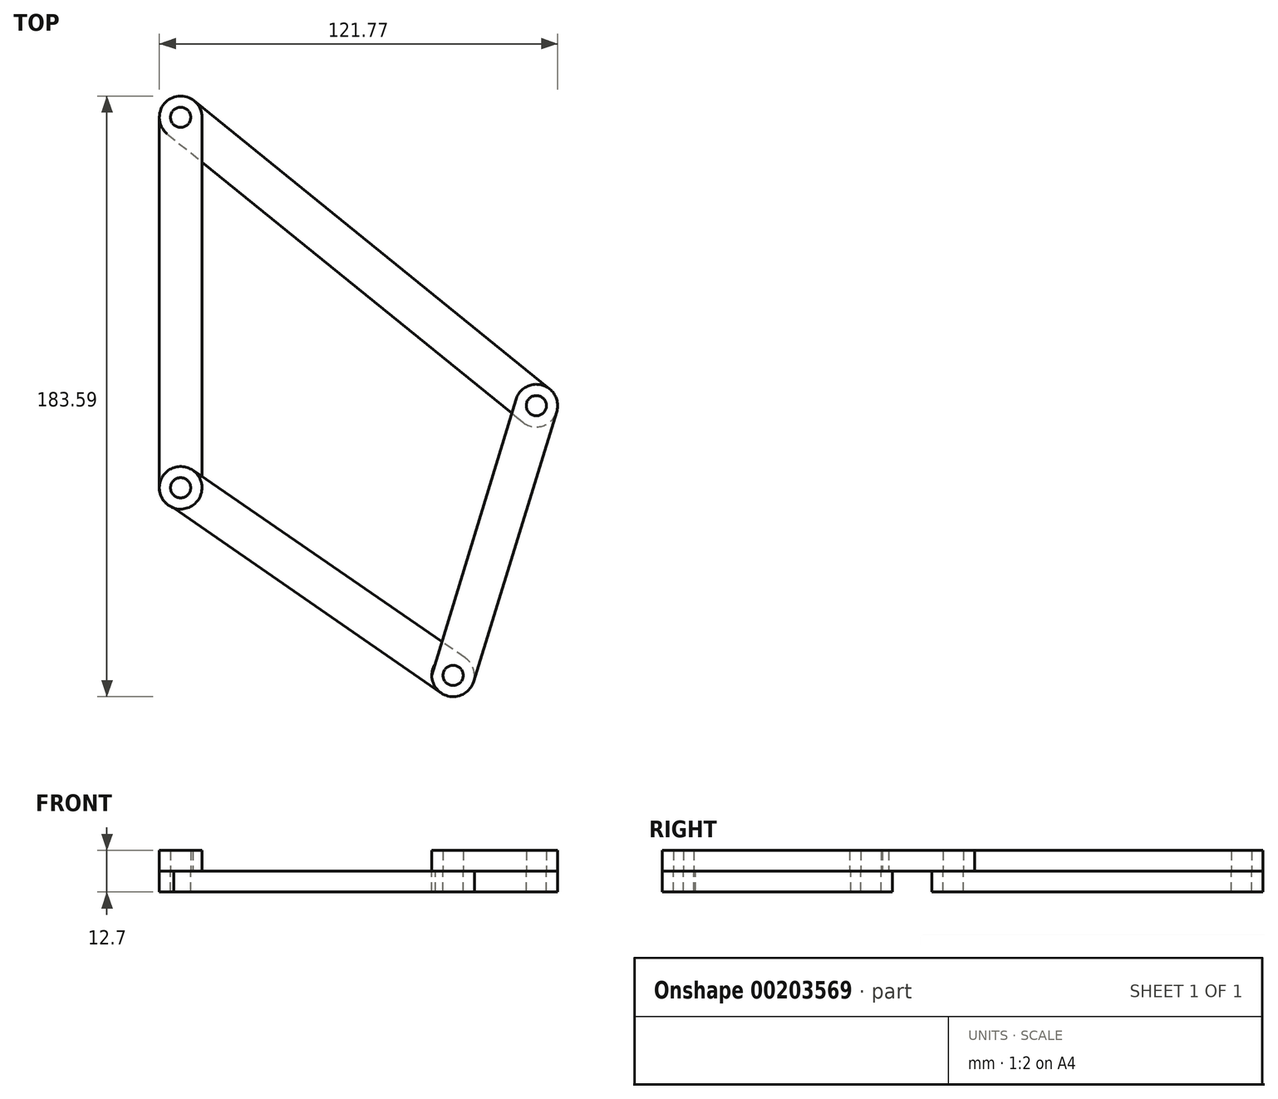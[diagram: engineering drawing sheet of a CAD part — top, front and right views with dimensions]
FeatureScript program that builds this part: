
annotation { "Feature Type Name" : "Feature", "Feature Type Description" : "" }
export const myFeature = defineFeature(function(context is Context, id is Id, definition is map)
    precondition{}
    {
        {
            var Q0;
            Q0=qCreatedBy(makeId("Top.planeOp"),FACE);
            var sketch = newSketch(context, id + "F0", { "sketchPlane" : qUnion([Q0])});
            skCircle(sketch, "E0", {"center": v(12.83, -29.92) * mm, "radius": 6.51 * mm});
            skCircle(sketch, "E1", {"center": v(-12.61, -112.37) * mm, "radius": 6.51 * mm});
            skCircle(sketch, "E2", {"center": v(-95.91, -55.04) * mm, "radius": 6.51 * mm});
            skCircle(sketch, "E3", {"center": v(-95.91, 58.2) * mm, "radius": 6.51 * mm});
            skLineSegment(sketch, "E4", {"start": v(-98.05, -61.2) * mm, "end": v(-16.32, -117.72) * mm});
            skLineSegment(sketch, "E5", {"start": v(-8.92, -107) * mm, "end": v(-92.22, -49.67) * mm});
            skLineSegment(sketch, "E6", {"start": v(-6.39, -114.29) * mm, "end": v(19.05, -31.84) * mm});
            skLineSegment(sketch, "E7", {"start": v(-19.12, -112.37) * mm, "end": v(6.6, -28.02) * mm});
            skLineSegment(sketch, "E8", {"start": v(16.93, -24.86) * mm, "end": v(-91.81, 63.26) * mm});
            skLineSegment(sketch, "E9", {"start": v(-100.01, 53.14) * mm, "end": v(8.72, -34.98) * mm});
            skLineSegment(sketch, "E10", {"start": v(-102.43, 58.2) * mm, "end": v(-102.43, -55.04) * mm});
            skLineSegment(sketch, "E11", {"start": v(-89.4, 58.2) * mm, "end": v(-89.4, -55.04) * mm});
            skCircle(sketch, "E12", {"center": v(-95.91, 58.2) * mm, "radius": 3.08 * mm});
            skCircle(sketch, "E13", {"center": v(12.83, -29.92) * mm, "radius": 3.08 * mm});
            skCircle(sketch, "E14", {"center": v(-12.61, -112.37) * mm, "radius": 3.08 * mm});
            skCircle(sketch, "E15", {"center": v(-95.91, -55.04) * mm, "radius": 3.08 * mm});
            skSolve(sketch);
        }
        {
            var Q0;
            Q0=makeQuery(id+"F0.imprint","IMPRINT",FACE,{"disambiguationData":[TD([[makeQuery(id+"F0.imprint","IMPRINT",EDGE,{"derivedFrom":sQuery(id+"F0.wireOp",EDGE,"E14")}),-1.0]])]});
            var Q1;
            {var subQ0=sQuery(id+"F0.wireOp",EDGE,"E5");var subQ1=sQuery(id+"F0.wireOp",EDGE,"E1");var subQ2=makeQuery(id+"F0.imprint","INTERSECT",VERTEX,{"derivedFrom":[subQ1,subQ0]});Q1=makeQuery(id+"F0.imprint","IMPRINT",FACE,{"disambiguationData":[TD([[makeQuery(id+"F0.imprint","IMPRINT",EDGE,{"disambiguationData":[TD([[subQ2,-1.0]])],"derivedFrom":subQ1}),-1.0]])]});}
            var Q2;
            {var subQ0=sQuery(id+"F0.wireOp",EDGE,"E6");Q2=makeQuery(id+"F0.imprint","IMPRINT",FACE,{"disambiguationData":[TD([[makeQuery(id+"F0.imprint","IMPRINT",EDGE,{"derivedFrom":subQ0}),1.0]])]});}
            var Q3;
            Q3=makeQuery(id+"F0.imprint","IMPRINT",FACE,{"disambiguationData":[TD([[makeQuery(id+"F0.imprint","IMPRINT",EDGE,{"derivedFrom":sQuery(id+"F0.wireOp",EDGE,"E13")}),-1.0]])]});
            var Q4;
            {var subQ0=sQuery(id+"F0.wireOp",EDGE,"E7");var subQ1=sQuery(id+"F0.wireOp",EDGE,"E0");var subQ2=makeQuery(id+"F0.imprint","INTERSECT",VERTEX,{"derivedFrom":[subQ1,subQ0]});Q4=makeQuery(id+"F0.imprint","IMPRINT",FACE,{"disambiguationData":[TD([[makeQuery(id+"F0.imprint","IMPRINT",EDGE,{"disambiguationData":[TD([[subQ2,-1.0]])],"derivedFrom":subQ1}),-1.0]])]});}
            var Q5;
            Q5=makeQuery(id+"F0.imprint","IMPRINT",FACE,{"disambiguationData":[TD([[makeQuery(id+"F0.imprint","IMPRINT",EDGE,{"derivedFrom":sQuery(id+"F0.wireOp",EDGE,"E15")}),-1.0]])]});
            var Q6;
            {var subQ9=sQuery(id+"F0.wireOp",EDGE,"E10");Q6=makeQuery(id+"F0.imprint","IMPRINT",FACE,{"disambiguationData":[TD([[makeQuery(id+"F0.imprint","IMPRINT",EDGE,{"derivedFrom":subQ9}),1.0]])]});}
            var Q7;
            Q7=makeQuery(id+"F0.imprint","IMPRINT",FACE,{"disambiguationData":[TD([[makeQuery(id+"F0.imprint","IMPRINT",EDGE,{"derivedFrom":sQuery(id+"F0.wireOp",EDGE,"E12")}),-1.0]])]});
            var Q8;
            {var subQ0=sQuery(id+"F0.wireOp",EDGE,"E9");var subQ1=sQuery(id+"F0.wireOp",EDGE,"E3");var subQ2=makeQuery(id+"F0.imprint","INTERSECT",VERTEX,{"derivedFrom":[subQ1,subQ0]});Q8=makeQuery(id+"F0.imprint","IMPRINT",FACE,{"disambiguationData":[TD([[makeQuery(id+"F0.imprint","IMPRINT",EDGE,{"disambiguationData":[TD([[subQ2,-1.0]])],"derivedFrom":subQ1}),-1.0]])]});}
            extrude(context, id + "F1", {"entities" : qUnion([Q0, Q1, Q2, Q3, Q4, Q5, Q6, Q7, Q8]), "depth" : 6.35 * mm});
        }
        {
            var Q0;
            Q0=makeQuery(id+"F0.imprint","IMPRINT",FACE,{"disambiguationData":[TD([[makeQuery(id+"F0.imprint","IMPRINT",EDGE,{"derivedFrom":sQuery(id+"F0.wireOp",EDGE,"E14")}),-1.0]])]});
            var Q1;
            {var subQ0=sQuery(id+"F0.wireOp",EDGE,"E4");Q1=makeQuery(id+"F0.imprint","IMPRINT",FACE,{"disambiguationData":[TD([[makeQuery(id+"F0.imprint","IMPRINT",EDGE,{"derivedFrom":subQ0}),1.0]])]});}
            var Q2;
            {var subQ0=sQuery(id+"F0.wireOp",EDGE,"E5");var subQ1=sQuery(id+"F0.wireOp",EDGE,"E1");var subQ2=makeQuery(id+"F0.imprint","INTERSECT",VERTEX,{"derivedFrom":[subQ1,subQ0]});Q2=makeQuery(id+"F0.imprint","IMPRINT",FACE,{"disambiguationData":[TD([[makeQuery(id+"F0.imprint","IMPRINT",EDGE,{"disambiguationData":[TD([[subQ2,-1.0]])],"derivedFrom":subQ1}),-1.0]])]});}
            var Q3;
            {var subQ0=sQuery(id+"F0.wireOp",EDGE,"E7");var subQ1=sQuery(id+"F0.wireOp",EDGE,"E1");var subQ2=makeQuery(id+"F0.imprint","INTERSECT",VERTEX,{"disambiguationData":[OD(0.0)],"derivedFrom":[subQ1,subQ0]});Q3=makeQuery(id+"F0.imprint","IMPRINT",FACE,{"disambiguationData":[TD([[makeQuery(id+"F0.imprint","IMPRINT",EDGE,{"disambiguationData":[TD([[subQ2,1.0]])],"derivedFrom":subQ1}),1.0]])]});}
            var Q4;
            Q4=makeQuery(id+"F0.imprint","IMPRINT",FACE,{"disambiguationData":[TD([[makeQuery(id+"F0.imprint","IMPRINT",EDGE,{"derivedFrom":sQuery(id+"F0.wireOp",EDGE,"E15")}),-1.0]])]});
            var Q5;
            {var subQ0=sQuery(id+"F0.wireOp",EDGE,"E5");var subQ1=sQuery(id+"F0.wireOp",EDGE,"E2");var subQ2=makeQuery(id+"F0.imprint","INTERSECT",VERTEX,{"derivedFrom":[subQ1,subQ0]});Q5=makeQuery(id+"F0.imprint","IMPRINT",FACE,{"disambiguationData":[TD([[makeQuery(id+"F0.imprint","IMPRINT",EDGE,{"disambiguationData":[TD([[subQ2,1.0]])],"derivedFrom":subQ1}),-1.0]])]});}
            var Q6;
            {var subQ0=sQuery(id+"F0.wireOp",EDGE,"E8");Q6=makeQuery(id+"F0.imprint","IMPRINT",FACE,{"disambiguationData":[TD([[makeQuery(id+"F0.imprint","IMPRINT",EDGE,{"derivedFrom":subQ0}),1.0]])]});}
            var Q7;
            Q7=makeQuery(id+"F0.imprint","IMPRINT",FACE,{"disambiguationData":[TD([[makeQuery(id+"F0.imprint","IMPRINT",EDGE,{"derivedFrom":sQuery(id+"F0.wireOp",EDGE,"E13")}),-1.0]])]});
            var Q8;
            {var subQ0=sQuery(id+"F0.wireOp",EDGE,"E7");var subQ1=sQuery(id+"F0.wireOp",EDGE,"E0");var subQ2=makeQuery(id+"F0.imprint","INTERSECT",VERTEX,{"derivedFrom":[subQ1,subQ0]});Q8=makeQuery(id+"F0.imprint","IMPRINT",FACE,{"disambiguationData":[TD([[makeQuery(id+"F0.imprint","IMPRINT",EDGE,{"disambiguationData":[TD([[subQ2,-1.0]])],"derivedFrom":subQ1}),-1.0]])]});}
            var Q9;
            {var subQ0=sQuery(id+"F0.wireOp",EDGE,"E9");var subQ1=sQuery(id+"F0.wireOp",EDGE,"E3");var subQ2=makeQuery(id+"F0.imprint","INTERSECT",VERTEX,{"derivedFrom":[subQ1,subQ0]});Q9=makeQuery(id+"F0.imprint","IMPRINT",FACE,{"disambiguationData":[TD([[makeQuery(id+"F0.imprint","IMPRINT",EDGE,{"disambiguationData":[TD([[subQ2,-1.0]])],"derivedFrom":subQ1}),-1.0]])]});}
            var Q10;
            Q10=makeQuery(id+"F0.imprint","IMPRINT",FACE,{"disambiguationData":[TD([[makeQuery(id+"F0.imprint","IMPRINT",EDGE,{"derivedFrom":sQuery(id+"F0.wireOp",EDGE,"E12")}),-1.0]])]});
            extrude(context, id + "F2", {"entities" : qUnion([Q0, Q1, Q2, Q3, Q4, Q5, Q6, Q7, Q8, Q9, Q10]), "oppositeDirection" : true, "depth" : 6.35 * mm});
        }
    });
